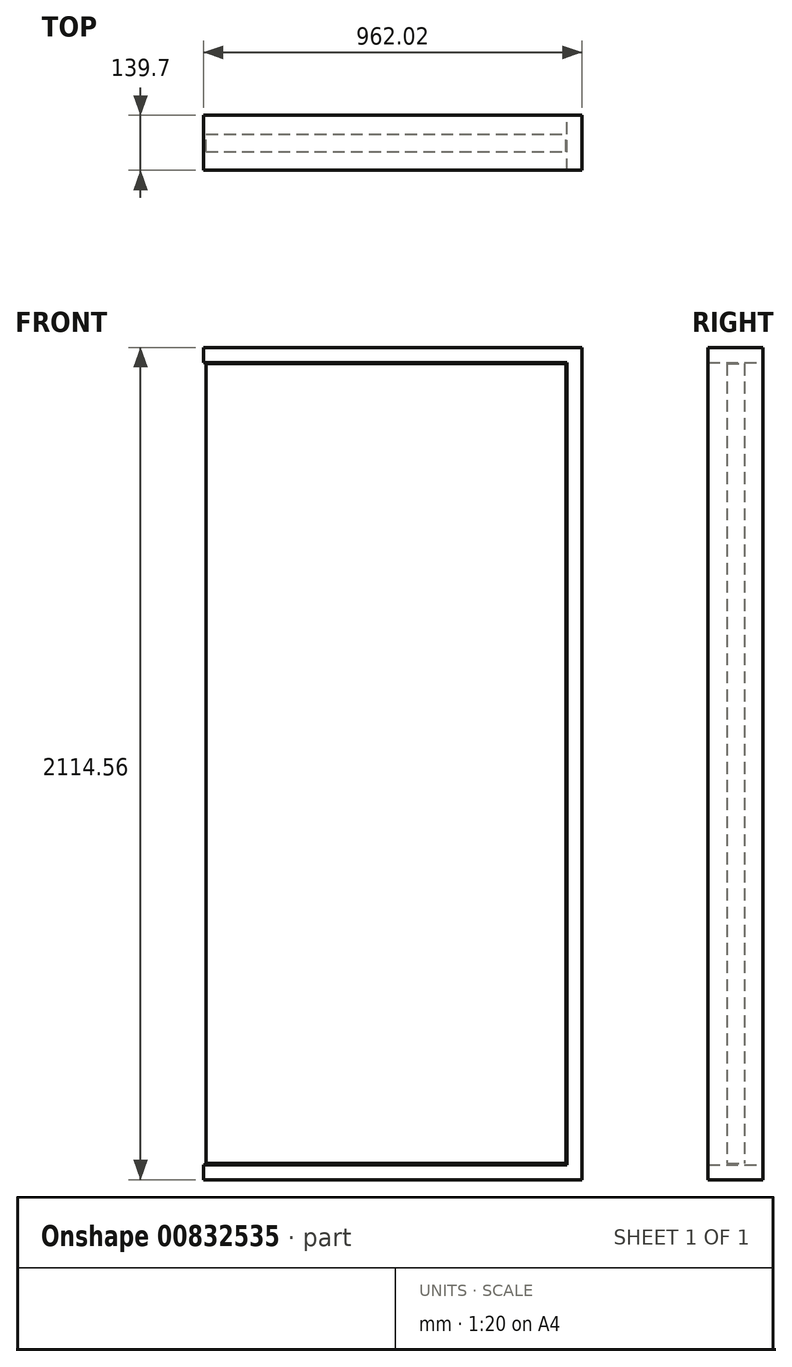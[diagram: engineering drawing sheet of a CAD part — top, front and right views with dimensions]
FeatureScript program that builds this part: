
annotation { "Feature Type Name" : "Feature", "Feature Type Description" : "" }
export const myFeature = defineFeature(function(context is Context, id is Id, definition is map)
    precondition{}
    {
        {
            var Q0;
            Q0=qCreatedBy(makeId("Front.planeOp"),FACE);
            var sketch = newSketch(context, id + "F0", { "sketchPlane" : qUnion([Q0])});
            skLineSegment(sketch, "E0.bottom", {"start": v(6.35, 2032) * mm, "end": v(920.75, 2032) * mm});
            skLineSegment(sketch, "E0.top", {"start": v(6.35, 0) * mm, "end": v(920.75, 0) * mm});
            skLineSegment(sketch, "E0.left", {"start": v(6.35, 2032) * mm, "end": v(6.35, 0) * mm});
            skLineSegment(sketch, "E0.right", {"start": v(920.75, 2032) * mm, "end": v(920.75, 0) * mm});
            skLineSegment(sketch, "E1", {"start": v(0, 0) * mm, "end": v(0, -824.44) * mm, "construction": true});
            skLineSegment(sketch, "E2.bottom", {"start": v(0, 2073.28) * mm, "end": v(962.02, 2073.28) * mm});
            skLineSegment(sketch, "E2.top", {"start": v(0, -41.27) * mm, "end": v(962.03, -41.27) * mm});
            skLineSegment(sketch, "E2.left", {"start": v(0, 2073.28) * mm, "end": v(0, 2035.18) * mm});
            skLineSegment(sketch, "E2.right", {"start": v(962.02, 2073.28) * mm, "end": v(962.03, -41.27) * mm});
            skLineSegment(sketch, "E3.bottom", {"start": v(0, 2035.18) * mm, "end": v(923.92, 2035.18) * mm});
            skLineSegment(sketch, "E3.top", {"start": v(0, -3.17) * mm, "end": v(923.93, -3.17) * mm});
            skLineSegment(sketch, "E3.right", {"start": v(923.92, 2035.18) * mm, "end": v(923.93, -3.17) * mm});
            skLineSegment(sketch, "E4.trimOffspring", {"start": v(0, -3.17) * mm, "end": v(0, -41.27) * mm});
            skSolve(sketch);
        }
        {
            var Q0;
            Q0=makeQuery(id+"F0.imprint","IMPRINT",FACE,{"disambiguationData":[TD([[makeQuery(id+"F0.imprint","IMPRINT",EDGE,{"derivedFrom":sQuery(id+"F0.wireOp",EDGE,"E0.bottom")}),-1.0]])]});
            extrude(context, id + "F1", {"entities" : qUnion([Q0]), "endBound" : BoundingType.SYMMETRIC, "depth" : 44.45 * mm, "offsetDistance" : 25.4 * mm});
        }
        {
            var Q0;
            Q0=makeQuery(id+"F0.imprint","IMPRINT",FACE,{"disambiguationData":[TD([[makeQuery(id+"F0.imprint","IMPRINT",EDGE,{"derivedFrom":sQuery(id+"F0.wireOp",EDGE,"E2.bottom")}),-1.0]])]});
            extrude(context, id + "F2", {"entities" : qUnion([Q0]), "endBound" : BoundingType.SYMMETRIC, "depth" : 139.7 * mm, "offsetDistance" : 25.4 * mm});
        }
    });
